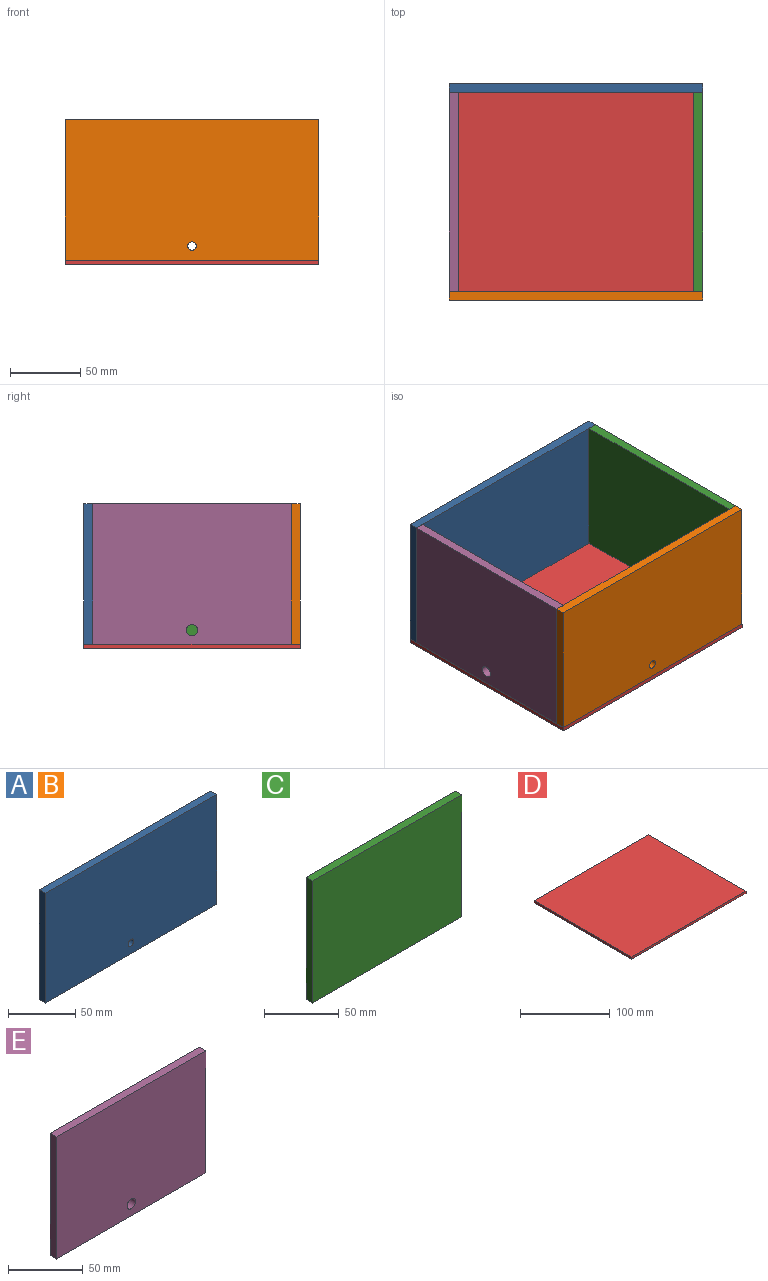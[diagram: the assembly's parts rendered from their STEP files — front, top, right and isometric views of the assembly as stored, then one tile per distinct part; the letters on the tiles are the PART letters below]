
ASSEMBLY  parts=5 mates=4
PART A: 7 faces, bbox 180x6.4x100 mm
  f0: plane 180x6.35mm, normal (0,0,1), area 1143mm2, adj f1,f3,f4,f5
  f1: plane 100x6.35mm, normal (-1,0,0), area 635mm2, adj f0,f2,f4,f5
  f2: plane 180x6.35mm, normal (0,0,-1), area 1143mm2, adj f1,f3,f4,f5
  f3: plane 100x6.35mm, normal (1,0,0), area 635mm2, adj f0,f2,f4,f5
  f4: plane 180x100mm, normal (0,-1,0), area 17971.7mm2, adj f0,f1,f2,f3,f6
  f5: plane 180x100mm, normal (0,1,0), area 17971.7mm2, adj f0,f1,f2,f3,f6
  f6: cylinder r=3mm len=6.35mm, axis (0,-1,0), area 119.7mm2, adj f4,f5
PART B: same geometry as A
PART C: 6 faces, bbox 141.3x6.4x100 mm
  f0: plane 141.3x6.35mm, normal (0,0,1), area 897.3mm2, adj f1,f3,f4,f5
  f1: plane 100x6.35mm, normal (-1,0,0), area 635mm2, adj f0,f2,f4,f5
  f2: plane 141.3x6.35mm, normal (0,0,-1), area 897.3mm2, adj f1,f3,f4,f5
  f3: plane 100x6.35mm, normal (1,0,0), area 635mm2, adj f0,f2,f4,f5
  f4: plane 141.3x100mm, normal (0,-1,0), area 14130mm2, adj f0,f1,f2,f3
  f5: plane 141.3x100mm, normal (0,1,0), area 14130mm2, adj f0,f1,f2,f3
PART D: 6 faces, bbox 180x154x3 mm
  f0: plane 180x3mm, normal (0,1,0), area 540mm2, adj f1,f3,f4,f5
  f1: plane 154x3mm, normal (-1,0,0), area 462mm2, adj f0,f2,f4,f5
  f2: plane 180x3mm, normal (0,-1,0), area 540mm2, adj f1,f3,f4,f5
  f3: plane 154x3mm, normal (1,0,0), area 462mm2, adj f0,f2,f4,f5
  f4: plane 180x154mm, normal (0,0,1), area 27720mm2, adj f0,f1,f2,f3
  f5: plane 180x154mm, normal (0,0,-1), area 27720mm2, adj f0,f1,f2,f3
PART E: 7 faces, bbox 141.3x6.4x100 mm
  f0: plane 141.3x6.35mm, normal (0,0,1), area 897.3mm2, adj f1,f3,f4,f5
  f1: plane 100x6.35mm, normal (-1,0,0), area 635mm2, adj f0,f2,f4,f5
  f2: plane 141.3x6.35mm, normal (0,0,-1), area 897.3mm2, adj f1,f3,f4,f5
  f3: plane 100x6.35mm, normal (1,0,0), area 635mm2, adj f0,f2,f4,f5
  f4: plane 141.3x100mm, normal (0,-1,0), area 14079.7mm2, adj f0,f1,f2,f3,f6
  f5: plane 141.3x100mm, normal (0,1,0), area 14079.7mm2, adj f0,f1,f2,f3,f6
  f6: cylinder r=4mm len=8mm, axis (0,-1,0), area 159.6mm2, adj f4,f5
PLACE A t=(-0.14,77,51.62)mm
PLACE B t=(-0.14,-70.65,51.62)mm
PLACE C rot(axis=(0,0,1),90deg) t=(83.51,0,51.62)mm
PLACE D t=(-0.14,0,-1.38)mm fixed
PLACE E rot(axis=(0,0,-1),90deg) t=(-83.79,0,51.62)mm
MATE fastened E.f1 <-> A.f4  axis (0,1,0) through (-90.14,70.65,1.62)mm
MATE fastened B.f4 <-> D.f2  axis (0,-1,0) through (-90.14,-77,1.62)mm
MATE fastened A.f5 <-> D.f0  axis (0,1,0) through (89.86,77,1.62)mm
MATE fastened C.f3 <-> A.f4  axis (0,1,0) through (89.86,70.65,1.62)mm
